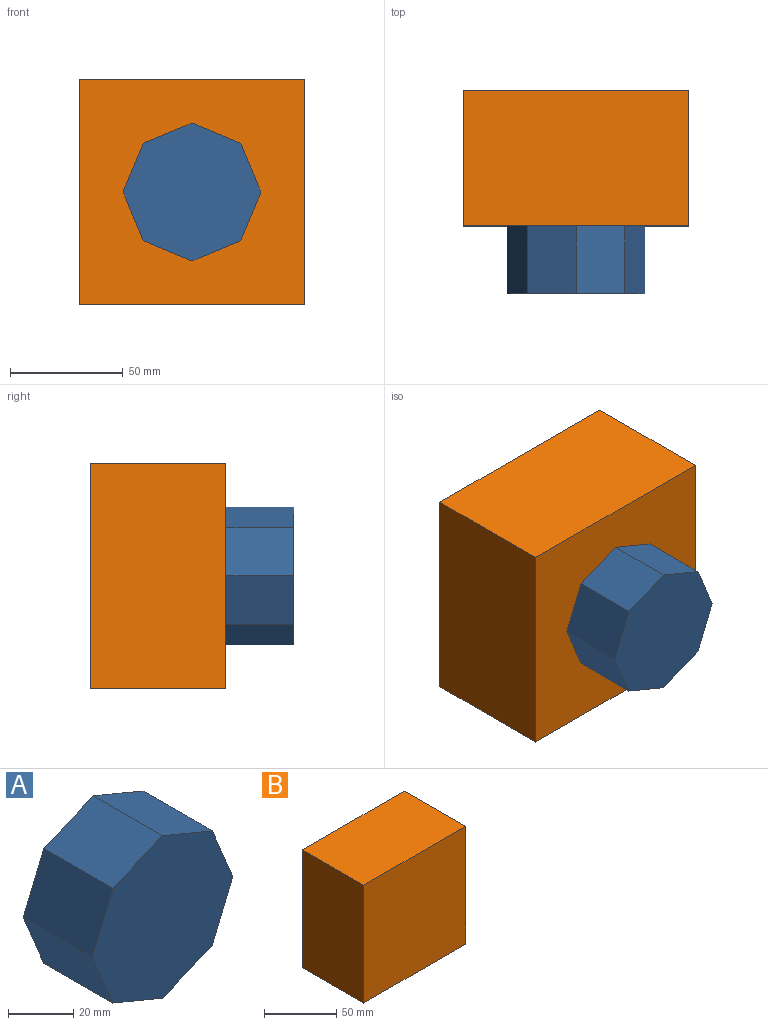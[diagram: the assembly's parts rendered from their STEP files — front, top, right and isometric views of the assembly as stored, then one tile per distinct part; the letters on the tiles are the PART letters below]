
ASSEMBLY  parts=2 mates=1
PART A: 10 faces, bbox 61x30x61 mm
  f0: plane 30x21.57mm, normal (-0.38,0,-0.92), area 700.5mm2, adj f1,f7,f8,f9
  f1: plane 30x21.58mm, normal (0.38,0,-0.92), area 700.5mm2, adj f0,f2,f8,f9
  f2: plane 30x21.57mm, normal (0.92,0,-0.38), area 700.5mm2, adj f1,f3,f8,f9
  f3: plane 30x21.58mm, normal (0.92,0,0.38), area 700.5mm2, adj f2,f4,f8,f9
  f4: plane 30x21.57mm, normal (0.38,0,0.92), area 700.5mm2, adj f3,f5,f8,f9
  f5: plane 30x21.58mm, normal (-0.38,0,0.92), area 700.5mm2, adj f4,f6,f8,f9
  f6: plane 30x21.57mm, normal (-0.92,0,0.38), area 700.5mm2, adj f5,f7,f8,f9
  f7: plane 30x21.58mm, normal (-0.92,0,-0.38), area 700.5mm2, adj f0,f6,f8,f9
  f8: plane 61.02x61.02mm, normal (0,-1,0), area 2632.9mm2, adj f0,f1,f2,f3,f4,f5,f6,f7
  f9: plane 61.02x61.02mm, normal (0,1,0), area 2632.9mm2, adj f0,f1,f2,f3,f4,f5,f6,f7
PART B: 6 faces, bbox 100x60x100 mm
  f0: plane 100x60mm, normal (-1,0,0), area 6000mm2, adj f1,f3,f4,f5
  f1: plane 100x60mm, normal (0,0,-1), area 6000mm2, adj f0,f2,f4,f5
  f2: plane 100x60mm, normal (1,0,0), area 6000mm2, adj f1,f3,f4,f5
  f3: plane 100x60mm, normal (0,0,1), area 6000mm2, adj f0,f2,f4,f5
  f4: plane 100x100mm, normal (0,-1,0), area 10000mm2, adj f0,f1,f2,f3
  f5: plane 100x100mm, normal (0,1,0), area 10000mm2, adj f0,f1,f2,f3
PLACE A t=(-45.78,-32.72,35.56)mm
PLACE B t=(-95.78,27.28,-14.44)mm
MATE slider A.f9 <-> B.f4  axis (0,1,0) through (-45.78,-32.72,35.56)mm
